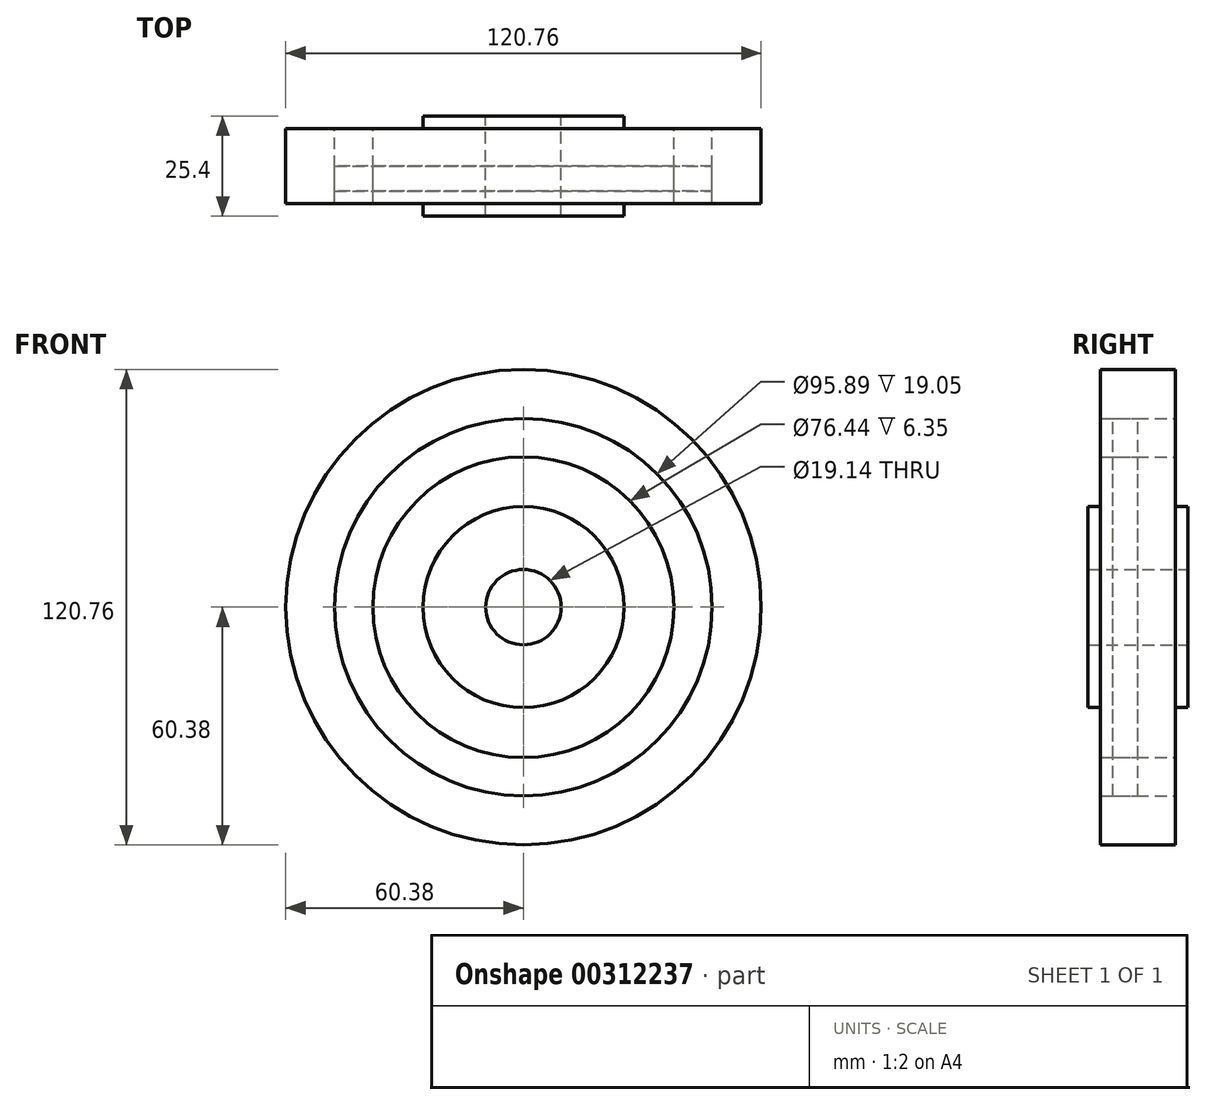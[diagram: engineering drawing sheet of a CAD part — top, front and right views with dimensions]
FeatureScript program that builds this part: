
annotation { "Feature Type Name" : "Feature", "Feature Type Description" : "" }
export const myFeature = defineFeature(function(context is Context, id is Id, definition is map)
    precondition{}
    {
        {
            var Q0;
            Q0=qCreatedBy(makeId("Front.planeOp"),FACE);
            var sketch = newSketch(context, id + "F0", { "sketchPlane" : qUnion([Q0])});
            skCircle(sketch, "E0", {"center": v(0, 0) * mm, "radius": 9.57 * mm});
            skCircle(sketch, "E1", {"center": v(0, 0) * mm, "radius": 25.53 * mm});
            skCircle(sketch, "E2", {"center": v(0, 0) * mm, "radius": 38.22 * mm});
            skCircle(sketch, "E3", {"center": v(0, 0) * mm, "radius": 47.94 * mm});
            skCircle(sketch, "E4", {"center": v(0, 0) * mm, "radius": 60.38 * mm});
            skSolve(sketch);
        }
        {
            var Q0;
            Q0=makeQuery(id+"F0.imprint","IMPRINT",FACE,{"disambiguationData":[TD([[makeQuery(id+"F0.imprint","IMPRINT",EDGE,{"derivedFrom":sQuery(id+"F0.wireOp",EDGE,"E0")}),-1.0]])]});
            extrude(context, id + "F1", {"entities" : qUnion([Q0]), "endBound" : BoundingType.SYMMETRIC, "depth" : 25.4 * mm});
        }
        {
            var Q0;
            Q0 = qSketchRegion(id + "F0", true);
            extrude(context, id + "F2", {"entities" : qUnion([Q0]), "endBound" : BoundingType.SYMMETRIC, "depth" : 19.05 * mm});
        }
        {
            var Q0;
            Q0=makeQuery(id+"F0.imprint","IMPRINT",FACE,{"disambiguationData":[TD([[makeQuery(id+"F0.imprint","IMPRINT",EDGE,{"derivedFrom":sQuery(id+"F0.wireOp",EDGE,"E1")}),-1.0]])]});
            extrude(context, id + "F3", {"entities" : qUnion([Q0]), "operationType" : NewBodyOperationType.ADD, "endBound" : BoundingType.SYMMETRIC, "depth" : 19.05 * mm});
        }
        {
            var Q0;
            Q0=makeQuery(id+"F0.imprint","IMPRINT",FACE,{"disambiguationData":[TD([[makeQuery(id+"F0.imprint","IMPRINT",EDGE,{"derivedFrom":sQuery(id+"F0.wireOp",EDGE,"E2")}),-1.0]])]});
            extrude(context, id + "F4", {"entities" : qUnion([Q0]), "depth" : 6.35 * mm});
        }
    });
